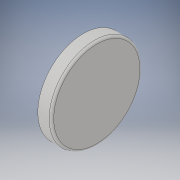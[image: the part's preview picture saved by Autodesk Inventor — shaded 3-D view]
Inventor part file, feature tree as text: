
AUTODESK INVENTOR PART (.ipt)
format: ipt  version: 2019 (Build 230136000, 136)  size: 107,008 bytes
history: native  units: mm
features: extrude x1, fillet x1, sketch x1
ambient origin geometry x8: Origin, YZ Plane, XZ Plane, XY Plane, X Axis, Y Axis, Z Axis, Center Point
bodies: Solid1 (feature_tree)
feature tree (3):
  extrude  "Extrusion1"  Depth=3.0mm TaperAngle=0.0deg
  fillet  "Fillet1"  Radius=0.5mm
  sketch  "Sketch1"  dims[d0=20.0mm d1=3.0mm d2=0.0mm d3=0.5mm]
